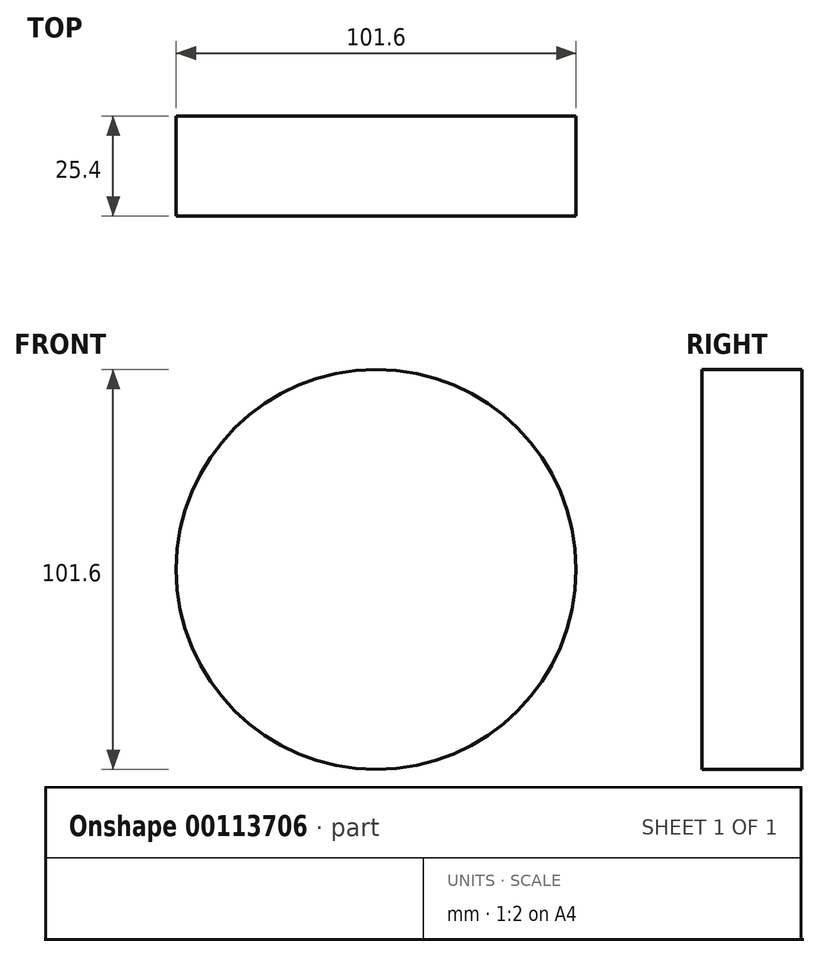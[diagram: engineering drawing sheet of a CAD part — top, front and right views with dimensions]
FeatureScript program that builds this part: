
annotation { "Feature Type Name" : "Feature", "Feature Type Description" : "" }
export const myFeature = defineFeature(function(context is Context, id is Id, definition is map)
    precondition{}
    {
        {
            var Q0;
            Q0=qCreatedBy(makeId("Front.planeOp"),FACE);
            var sketch = newSketch(context, id + "F0", { "sketchPlane" : qUnion([Q0])});
            skCircle(sketch, "E0", {"center": v(0, 0) * mm, "radius": 50.8 * mm});
            skSolve(sketch);
        }
        {
            var Q0;
            Q0 = qSketchRegion(id + "F0", true);
            extrude(context, id + "F1", {"entities" : qUnion([Q0]), "depth" : 25.4 * mm});
        }
    });
